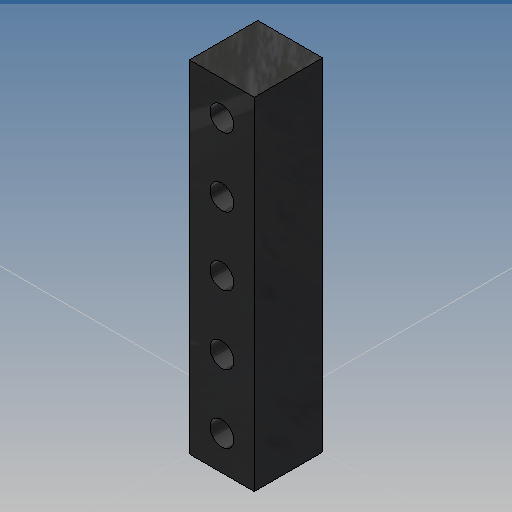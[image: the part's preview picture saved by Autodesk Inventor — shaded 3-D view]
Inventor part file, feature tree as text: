
AUTODESK INVENTOR PART (.ipt)
format: ipt  version: 2019 (Build 230136000, 136)  size: 124,928 bytes
history: native  units: in
note: dims shown in document units (in); Inventor stores cm internally (conversion verified against a paired STEP export)
features: extrude x1, sketch x1
ambient origin geometry x8: Origin, YZ Plane, XZ Plane, XY Plane, X Axis, Y Axis, Z Axis, Center Point
bodies: Solid1 (feature_tree)
feature tree (2):
  extrude  "Extrusion1"  Depth=0.5in
  sketch  "Sketch1"  dims[d0=0.095in d1=0.5in d2=0.035in d3=0.035in d4=0.035in d5=0.05in d6=0.1in d7=0.1in d8=0.035in d9=0.035in d10=0.1in d11=0.1in d12=0.0475in d13=0.1in d14=0.0in]
